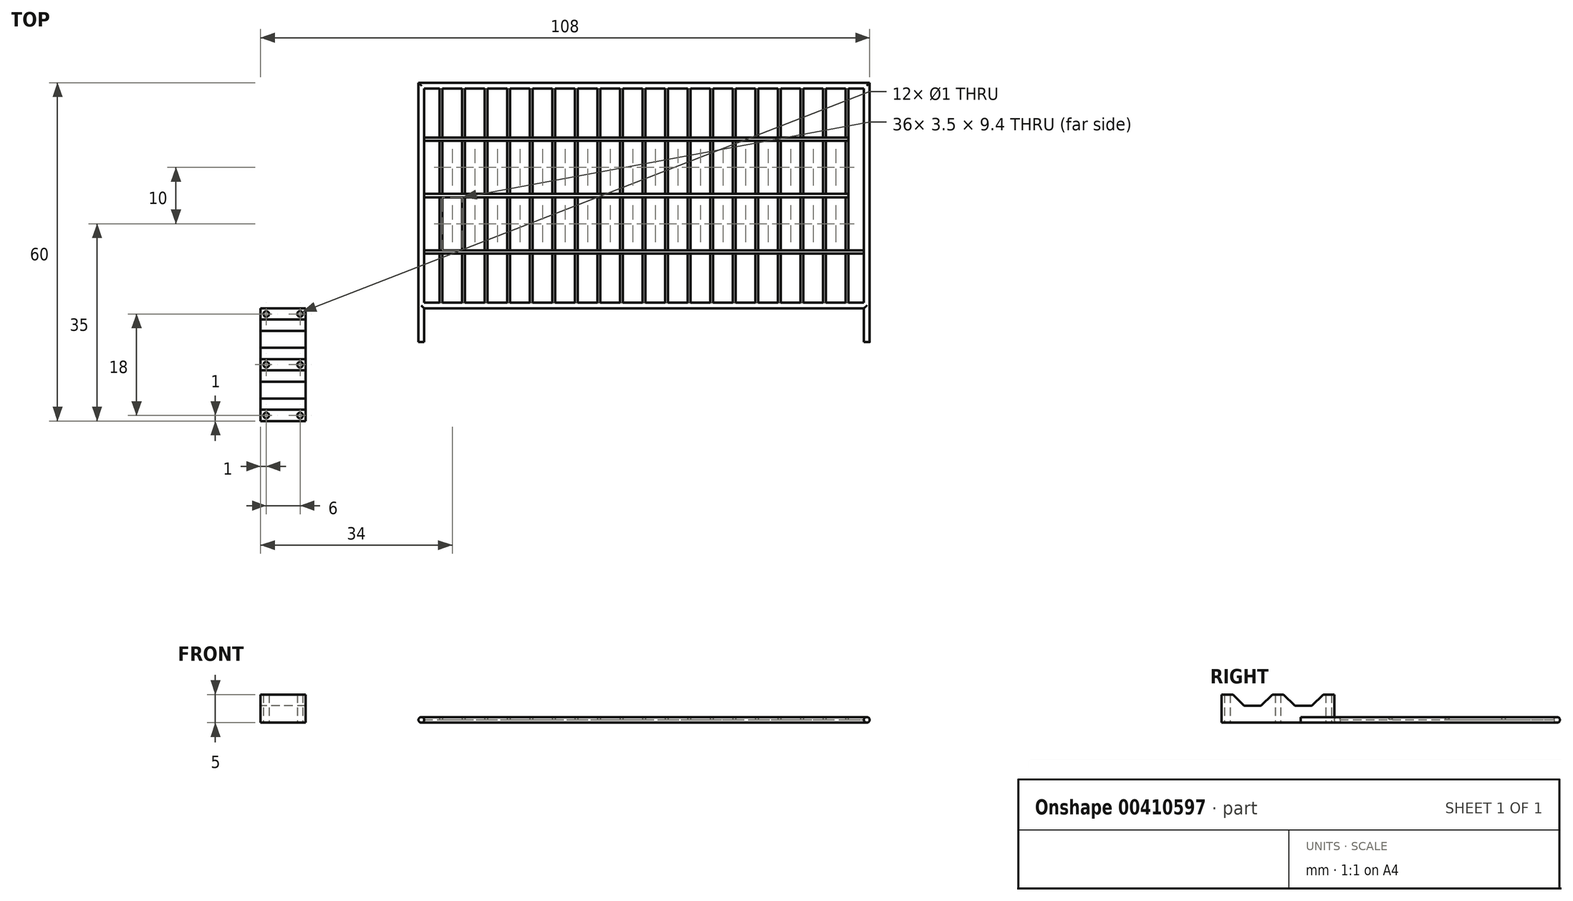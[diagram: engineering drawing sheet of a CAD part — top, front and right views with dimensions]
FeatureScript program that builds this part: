
annotation { "Feature Type Name" : "Feature", "Feature Type Description" : "" }
export const myFeature = defineFeature(function(context is Context, id is Id, definition is map)
    precondition{}
    {
        {
            var Q0;
            Q0=qCreatedBy(makeId("Top.planeOp"),FACE);
            var sketch = newSketch(context, id + "F0", { "sketchPlane" : qUnion([Q0])});
            skLineSegment(sketch, "E0.bottom", {"start": v(0, 0) * mm, "end": v(80, 0) * mm});
            skLineSegment(sketch, "E0.top", {"start": v(0, 40) * mm, "end": v(80, 40) * mm});
            skLineSegment(sketch, "E0.left", {"start": v(0, 0) * mm, "end": v(0, 40) * mm});
            skLineSegment(sketch, "E0.right", {"start": v(80, 0) * mm, "end": v(80, 40) * mm});
            skLineSegment(sketch, "E1", {"start": v(0, 0) * mm, "end": v(0, -6) * mm});
            skLineSegment(sketch, "E2", {"start": v(0, -6) * mm, "end": v(1, -6) * mm});
            skLineSegment(sketch, "E3", {"start": v(1, -6) * mm, "end": v(1, 0) * mm});
            skLineSegment(sketch, "E4", {"start": v(1, 39) * mm, "end": v(79, 39) * mm});
            skLineSegment(sketch, "E5", {"start": v(79, 39) * mm, "end": v(79, 1) * mm});
            skLineSegment(sketch, "E6", {"start": v(79, -6) * mm, "end": v(80, -6) * mm});
            skLineSegment(sketch, "E7", {"start": v(80, -6) * mm, "end": v(80, 0) * mm});
            skLineSegment(sketch, "E8", {"start": v(1, 1) * mm, "end": v(79, 1) * mm});
            skLineSegment(sketch, "E9.trimOffspring", {"start": v(79, 0) * mm, "end": v(79, -6) * mm});
            skLineSegment(sketch, "E10.trimOffspring", {"start": v(1, 1) * mm, "end": v(1, 39) * mm});
            skSolve(sketch);
        }
        {
            var Q0;
            Q0 = qSketchRegion(id + "F0", true);
            extrude(context, id + "F1", {"entities" : qUnion([Q0]), "depth" : 1 * mm});
        }
        {
            var Q0;
            Q0=makeQuery(id+"F1.opExtrude","CAP_FACE",FACE,{"disambiguationData":[OSD([sQuery(id+"F0.wireOp",EDGE,"E0.bottom"),sQuery(id+"F0.wireOp",EDGE,"E0.top"),sQuery(id+"F0.wireOp",EDGE,"E0.left"),sQuery(id+"F0.wireOp",EDGE,"E0.right"),sQuery(id+"F0.wireOp",EDGE,"E1"),sQuery(id+"F0.wireOp",EDGE,"E2"),sQuery(id+"F0.wireOp",EDGE,"E3"),sQuery(id+"F0.wireOp",EDGE,"E4"),sQuery(id+"F0.wireOp",EDGE,"E5"),sQuery(id+"F0.wireOp",EDGE,"E6"),sQuery(id+"F0.wireOp",EDGE,"E7"),sQuery(id+"F0.wireOp",EDGE,"E8"),sQuery(id+"F0.wireOp",EDGE,"E9.trimOffspring"),sQuery(id+"F0.wireOp",EDGE,"E10.trimOffspring")])],"isStart":false});
            var sketch = newSketch(context, id + "F2", { "sketchPlane" : qUnion([Q0])});
            skLineSegment(sketch, "E11", {"start": v(40, 1) * mm, "end": v(40, 39) * mm, "construction": true});
            skLineSegment(sketch, "E12", {"start": v(40.25, 1) * mm, "end": v(40.25, 39) * mm});
            skLineSegment(sketch, "E13.MirrorCS", {"start": v(39.75, 1) * mm, "end": v(39.75, 39) * mm});
            skLineSegment(sketch, "E14.1.0.0", {"start": v(44.25, 1) * mm, "end": v(44.25, 39) * mm});
            skLineSegment(sketch, "E14.1.0.1", {"start": v(43.75, 1) * mm, "end": v(43.75, 39) * mm});
            skLineSegment(sketch, "E14.2.0.0", {"start": v(48.25, 1) * mm, "end": v(48.25, 39) * mm});
            skLineSegment(sketch, "E14.2.0.1", {"start": v(47.75, 1) * mm, "end": v(47.75, 39) * mm});
            skLineSegment(sketch, "E14.3.0.0", {"start": v(52.25, 1) * mm, "end": v(52.25, 39) * mm});
            skLineSegment(sketch, "E14.3.0.1", {"start": v(51.75, 1) * mm, "end": v(51.75, 39) * mm});
            skLineSegment(sketch, "E14.4.0.0", {"start": v(56.25, 1) * mm, "end": v(56.25, 39) * mm});
            skLineSegment(sketch, "E14.4.0.1", {"start": v(55.75, 1) * mm, "end": v(55.75, 39) * mm});
            skLineSegment(sketch, "E14.5.0.0", {"start": v(60.25, 1) * mm, "end": v(60.25, 39) * mm});
            skLineSegment(sketch, "E14.5.0.1", {"start": v(59.75, 1) * mm, "end": v(59.75, 39) * mm});
            skLineSegment(sketch, "E14.6.0.0", {"start": v(64.25, 1) * mm, "end": v(64.25, 39) * mm});
            skLineSegment(sketch, "E14.6.0.1", {"start": v(63.75, 1) * mm, "end": v(63.75, 39) * mm});
            skLineSegment(sketch, "E14.7.0.0", {"start": v(68.25, 1) * mm, "end": v(68.25, 39) * mm});
            skLineSegment(sketch, "E14.7.0.1", {"start": v(67.75, 1) * mm, "end": v(67.75, 39) * mm});
            skLineSegment(sketch, "E14.8.0.0", {"start": v(72.25, 1) * mm, "end": v(72.25, 39) * mm});
            skLineSegment(sketch, "E14.8.0.1", {"start": v(71.75, 1) * mm, "end": v(71.75, 39) * mm});
            skLineSegment(sketch, "E14.9.0.0", {"start": v(76.25, 1) * mm, "end": v(76.25, 39) * mm});
            skLineSegment(sketch, "E14.9.0.1", {"start": v(75.75, 1) * mm, "end": v(75.75, 39) * mm});
            skLineSegment(sketch, "E14.direction1", {"start": v(40.25, 1) * mm, "end": v(44.25, 1) * mm, "construction": true});
            skLineSegment(sketch, "E15.MirrorCS", {"start": v(36.25, 1) * mm, "end": v(36.25, 39) * mm});
            skLineSegment(sketch, "E16.MirrorCS", {"start": v(35.75, 1) * mm, "end": v(35.75, 39) * mm});
            skLineSegment(sketch, "E17.MirrorCS", {"start": v(32.25, 1) * mm, "end": v(32.25, 39) * mm});
            skLineSegment(sketch, "E18.MirrorCS", {"start": v(31.75, 1) * mm, "end": v(31.75, 39) * mm});
            skLineSegment(sketch, "E19.MirrorCS", {"start": v(28.25, 1) * mm, "end": v(28.25, 39) * mm});
            skLineSegment(sketch, "E20.MirrorCS", {"start": v(27.75, 1) * mm, "end": v(27.75, 39) * mm});
            skLineSegment(sketch, "E21.MirrorCS", {"start": v(24.25, 1) * mm, "end": v(24.25, 39) * mm});
            skLineSegment(sketch, "E22.MirrorCS", {"start": v(23.75, 1) * mm, "end": v(23.75, 39) * mm});
            skLineSegment(sketch, "E23.MirrorCS", {"start": v(20.25, 1) * mm, "end": v(20.25, 39) * mm});
            skLineSegment(sketch, "E24.MirrorCS", {"start": v(19.75, 1) * mm, "end": v(19.75, 39) * mm});
            skLineSegment(sketch, "E25.MirrorCS", {"start": v(16.25, 1) * mm, "end": v(16.25, 39) * mm});
            skLineSegment(sketch, "E26.MirrorCS", {"start": v(15.75, 1) * mm, "end": v(15.75, 39) * mm});
            skLineSegment(sketch, "E27.MirrorCS", {"start": v(12.25, 1) * mm, "end": v(12.25, 39) * mm});
            skLineSegment(sketch, "E28.MirrorCS", {"start": v(11.75, 1) * mm, "end": v(11.75, 39) * mm});
            skLineSegment(sketch, "E29.MirrorCS", {"start": v(7.75, 1) * mm, "end": v(7.75, 39) * mm});
            skLineSegment(sketch, "E30.MirrorCS", {"start": v(8.25, 1) * mm, "end": v(8.25, 39) * mm});
            skLineSegment(sketch, "E31.MirrorCS", {"start": v(4.25, 1) * mm, "end": v(4.25, 39) * mm});
            skLineSegment(sketch, "E32.MirrorCS", {"start": v(3.75, 1) * mm, "end": v(3.75, 39) * mm});
            skLineSegment(sketch, "E33", {"start": v(3.75, 39) * mm, "end": v(76.25, 39) * mm});
            skLineSegment(sketch, "E34", {"start": v(3.75, 1) * mm, "end": v(76.25, 1) * mm});
            skSolve(sketch);
        }
        {
            var Q0;
            {var subQ0=sQuery(id+"F2.wireOp",EDGE,"E12");Q0=makeQuery(id+"F2.imprint","IMPRINT",FACE,{"disambiguationData":[TD([[makeQuery(id+"F2.imprint","IMPRINT",EDGE,{"derivedFrom":subQ0}),1.0]])]});}
            var Q1;
            {var subQ0=sQuery(id+"F2.wireOp",EDGE,"E14.1.0.0");Q1=makeQuery(id+"F2.imprint","IMPRINT",FACE,{"disambiguationData":[TD([[makeQuery(id+"F2.imprint","IMPRINT",EDGE,{"derivedFrom":subQ0}),1.0]])]});}
            var Q2;
            {var subQ0=sQuery(id+"F2.wireOp",EDGE,"E14.2.0.0");Q2=makeQuery(id+"F2.imprint","IMPRINT",FACE,{"disambiguationData":[TD([[makeQuery(id+"F2.imprint","IMPRINT",EDGE,{"derivedFrom":subQ0}),1.0]])]});}
            var Q3;
            {var subQ0=sQuery(id+"F2.wireOp",EDGE,"E14.3.0.0");Q3=makeQuery(id+"F2.imprint","IMPRINT",FACE,{"disambiguationData":[TD([[makeQuery(id+"F2.imprint","IMPRINT",EDGE,{"derivedFrom":subQ0}),1.0]])]});}
            var Q4;
            {var subQ0=sQuery(id+"F2.wireOp",EDGE,"E14.4.0.0");Q4=makeQuery(id+"F2.imprint","IMPRINT",FACE,{"disambiguationData":[TD([[makeQuery(id+"F2.imprint","IMPRINT",EDGE,{"derivedFrom":subQ0}),1.0]])]});}
            var Q5;
            {var subQ0=sQuery(id+"F2.wireOp",EDGE,"E14.5.0.0");Q5=makeQuery(id+"F2.imprint","IMPRINT",FACE,{"disambiguationData":[TD([[makeQuery(id+"F2.imprint","IMPRINT",EDGE,{"derivedFrom":subQ0}),1.0]])]});}
            var Q6;
            {var subQ0=sQuery(id+"F2.wireOp",EDGE,"E14.6.0.0");Q6=makeQuery(id+"F2.imprint","IMPRINT",FACE,{"disambiguationData":[TD([[makeQuery(id+"F2.imprint","IMPRINT",EDGE,{"derivedFrom":subQ0}),1.0]])]});}
            var Q7;
            {var subQ0=sQuery(id+"F2.wireOp",EDGE,"E14.7.0.0");Q7=makeQuery(id+"F2.imprint","IMPRINT",FACE,{"disambiguationData":[TD([[makeQuery(id+"F2.imprint","IMPRINT",EDGE,{"derivedFrom":subQ0}),1.0]])]});}
            var Q8;
            {var subQ0=sQuery(id+"F2.wireOp",EDGE,"E14.8.0.0");Q8=makeQuery(id+"F2.imprint","IMPRINT",FACE,{"disambiguationData":[TD([[makeQuery(id+"F2.imprint","IMPRINT",EDGE,{"derivedFrom":subQ0}),1.0]])]});}
            var Q9;
            {var subQ0=sQuery(id+"F2.wireOp",EDGE,"E14.9.0.0");Q9=makeQuery(id+"F2.imprint","IMPRINT",FACE,{"disambiguationData":[TD([[makeQuery(id+"F2.imprint","IMPRINT",EDGE,{"derivedFrom":subQ0}),1.0]])]});}
            var Q10;
            {var subQ0=sQuery(id+"F2.wireOp",EDGE,"E15.MirrorCS");Q10=makeQuery(id+"F2.imprint","IMPRINT",FACE,{"disambiguationData":[TD([[makeQuery(id+"F2.imprint","IMPRINT",EDGE,{"derivedFrom":subQ0}),1.0]])]});}
            var Q11;
            {var subQ0=sQuery(id+"F2.wireOp",EDGE,"E17.MirrorCS");Q11=makeQuery(id+"F2.imprint","IMPRINT",FACE,{"disambiguationData":[TD([[makeQuery(id+"F2.imprint","IMPRINT",EDGE,{"derivedFrom":subQ0}),1.0]])]});}
            var Q12;
            {var subQ0=sQuery(id+"F2.wireOp",EDGE,"E19.MirrorCS");Q12=makeQuery(id+"F2.imprint","IMPRINT",FACE,{"disambiguationData":[TD([[makeQuery(id+"F2.imprint","IMPRINT",EDGE,{"derivedFrom":subQ0}),1.0]])]});}
            var Q13;
            {var subQ0=sQuery(id+"F2.wireOp",EDGE,"E21.MirrorCS");Q13=makeQuery(id+"F2.imprint","IMPRINT",FACE,{"disambiguationData":[TD([[makeQuery(id+"F2.imprint","IMPRINT",EDGE,{"derivedFrom":subQ0}),1.0]])]});}
            var Q14;
            {var subQ0=sQuery(id+"F2.wireOp",EDGE,"E23.MirrorCS");Q14=makeQuery(id+"F2.imprint","IMPRINT",FACE,{"disambiguationData":[TD([[makeQuery(id+"F2.imprint","IMPRINT",EDGE,{"derivedFrom":subQ0}),1.0]])]});}
            var Q15;
            {var subQ0=sQuery(id+"F2.wireOp",EDGE,"E25.MirrorCS");Q15=makeQuery(id+"F2.imprint","IMPRINT",FACE,{"disambiguationData":[TD([[makeQuery(id+"F2.imprint","IMPRINT",EDGE,{"derivedFrom":subQ0}),1.0]])]});}
            var Q16;
            {var subQ0=sQuery(id+"F2.wireOp",EDGE,"E27.MirrorCS");Q16=makeQuery(id+"F2.imprint","IMPRINT",FACE,{"disambiguationData":[TD([[makeQuery(id+"F2.imprint","IMPRINT",EDGE,{"derivedFrom":subQ0}),1.0]])]});}
            var Q17;
            {var subQ0=sQuery(id+"F2.wireOp",EDGE,"E29.MirrorCS");Q17=makeQuery(id+"F2.imprint","IMPRINT",FACE,{"disambiguationData":[TD([[makeQuery(id+"F2.imprint","IMPRINT",EDGE,{"derivedFrom":subQ0}),-1.0]])]});}
            var Q18;
            {var subQ0=sQuery(id+"F2.wireOp",EDGE,"E31.MirrorCS");Q18=makeQuery(id+"F2.imprint","IMPRINT",FACE,{"disambiguationData":[TD([[makeQuery(id+"F2.imprint","IMPRINT",EDGE,{"derivedFrom":subQ0}),1.0]])]});}
            extrude(context, id + "F3", {"entities" : qUnion([Q0, Q1, Q2, Q3, Q4, Q5, Q6, Q7, Q8, Q9, Q10, Q11, Q12, Q13, Q14, Q15, Q16, Q17, Q18]), "operationType" : NewBodyOperationType.ADD, "oppositeDirection" : true, "depth" : 0.5 * mm});
        }
        {
            var Q0;
            {var subQ0=sQuery(id+"F2.wireOp",EDGE,"E34");var subQ1=sQuery(id+"F2.wireOp",EDGE,"E33");Q0=makeQuery(id+"F3.boolean.opBoolean","MERGE",FACE,{"derivedFrom":[makeQuery(id+"F1.opExtrude","CAP_FACE",FACE,{"disambiguationData":[OSD([sQuery(id+"F0.wireOp",EDGE,"E0.bottom"),sQuery(id+"F0.wireOp",EDGE,"E0.top"),sQuery(id+"F0.wireOp",EDGE,"E0.left"),sQuery(id+"F0.wireOp",EDGE,"E0.right"),sQuery(id+"F0.wireOp",EDGE,"E1"),sQuery(id+"F0.wireOp",EDGE,"E2"),sQuery(id+"F0.wireOp",EDGE,"E3"),sQuery(id+"F0.wireOp",EDGE,"E4"),sQuery(id+"F0.wireOp",EDGE,"E5"),sQuery(id+"F0.wireOp",EDGE,"E6"),sQuery(id+"F0.wireOp",EDGE,"E7"),sQuery(id+"F0.wireOp",EDGE,"E8"),sQuery(id+"F0.wireOp",EDGE,"E9.trimOffspring"),sQuery(id+"F0.wireOp",EDGE,"E10.trimOffspring")])],"isStart":false}),makeQuery(id+"F3.opExtrude","CAP_FACE",FACE,{"disambiguationData":[OSD([sQuery(id+"F2.wireOp",EDGE,"E12"),sQuery(id+"F2.wireOp",EDGE,"E13.MirrorCS"),subQ1,subQ0])],"isStart":true}),makeQuery(id+"F3.opExtrude","CAP_FACE",FACE,{"disambiguationData":[OSD([sQuery(id+"F2.wireOp",EDGE,"E14.1.0.0"),sQuery(id+"F2.wireOp",EDGE,"E14.1.0.1"),subQ1,subQ0])],"isStart":true}),makeQuery(id+"F3.opExtrude","CAP_FACE",FACE,{"disambiguationData":[OSD([sQuery(id+"F2.wireOp",EDGE,"E14.2.0.0"),sQuery(id+"F2.wireOp",EDGE,"E14.2.0.1"),subQ1,subQ0])],"isStart":true}),makeQuery(id+"F3.opExtrude","CAP_FACE",FACE,{"disambiguationData":[OSD([sQuery(id+"F2.wireOp",EDGE,"E14.3.0.0"),sQuery(id+"F2.wireOp",EDGE,"E14.3.0.1"),subQ1,subQ0])],"isStart":true}),makeQuery(id+"F3.opExtrude","CAP_FACE",FACE,{"disambiguationData":[OSD([sQuery(id+"F2.wireOp",EDGE,"E14.4.0.0"),sQuery(id+"F2.wireOp",EDGE,"E14.4.0.1"),subQ1,subQ0])],"isStart":true}),makeQuery(id+"F3.opExtrude","CAP_FACE",FACE,{"disambiguationData":[OSD([sQuery(id+"F2.wireOp",EDGE,"E14.5.0.0"),sQuery(id+"F2.wireOp",EDGE,"E14.5.0.1"),subQ1,subQ0])],"isStart":true}),makeQuery(id+"F3.opExtrude","CAP_FACE",FACE,{"disambiguationData":[OSD([sQuery(id+"F2.wireOp",EDGE,"E14.6.0.0"),sQuery(id+"F2.wireOp",EDGE,"E14.6.0.1"),subQ1,subQ0])],"isStart":true}),makeQuery(id+"F3.opExtrude","CAP_FACE",FACE,{"disambiguationData":[OSD([sQuery(id+"F2.wireOp",EDGE,"E14.7.0.0"),sQuery(id+"F2.wireOp",EDGE,"E14.7.0.1"),subQ1,subQ0])],"isStart":true}),makeQuery(id+"F3.opExtrude","CAP_FACE",FACE,{"disambiguationData":[OSD([sQuery(id+"F2.wireOp",EDGE,"E14.8.0.0"),sQuery(id+"F2.wireOp",EDGE,"E14.8.0.1"),subQ1,subQ0])],"isStart":true}),makeQuery(id+"F3.opExtrude","CAP_FACE",FACE,{"disambiguationData":[OSD([sQuery(id+"F2.wireOp",EDGE,"E14.9.0.0"),sQuery(id+"F2.wireOp",EDGE,"E14.9.0.1"),subQ1,subQ0])],"isStart":true}),makeQuery(id+"F3.opExtrude","CAP_FACE",FACE,{"disambiguationData":[OSD([sQuery(id+"F2.wireOp",EDGE,"E15.MirrorCS"),sQuery(id+"F2.wireOp",EDGE,"E16.MirrorCS"),subQ1,subQ0])],"isStart":true}),makeQuery(id+"F3.opExtrude","CAP_FACE",FACE,{"disambiguationData":[OSD([sQuery(id+"F2.wireOp",EDGE,"E17.MirrorCS"),sQuery(id+"F2.wireOp",EDGE,"E18.MirrorCS"),subQ1,subQ0])],"isStart":true}),makeQuery(id+"F3.opExtrude","CAP_FACE",FACE,{"disambiguationData":[OSD([sQuery(id+"F2.wireOp",EDGE,"E19.MirrorCS"),sQuery(id+"F2.wireOp",EDGE,"E20.MirrorCS"),subQ1,subQ0])],"isStart":true}),makeQuery(id+"F3.opExtrude","CAP_FACE",FACE,{"disambiguationData":[OSD([sQuery(id+"F2.wireOp",EDGE,"E21.MirrorCS"),sQuery(id+"F2.wireOp",EDGE,"E22.MirrorCS"),subQ1,subQ0])],"isStart":true}),makeQuery(id+"F3.opExtrude","CAP_FACE",FACE,{"disambiguationData":[OSD([sQuery(id+"F2.wireOp",EDGE,"E23.MirrorCS"),sQuery(id+"F2.wireOp",EDGE,"E24.MirrorCS"),subQ1,subQ0])],"isStart":true}),makeQuery(id+"F3.opExtrude","CAP_FACE",FACE,{"disambiguationData":[OSD([sQuery(id+"F2.wireOp",EDGE,"E25.MirrorCS"),sQuery(id+"F2.wireOp",EDGE,"E26.MirrorCS"),subQ1,subQ0])],"isStart":true}),makeQuery(id+"F3.opExtrude","CAP_FACE",FACE,{"disambiguationData":[OSD([sQuery(id+"F2.wireOp",EDGE,"E27.MirrorCS"),sQuery(id+"F2.wireOp",EDGE,"E28.MirrorCS"),subQ1,subQ0])],"isStart":true}),makeQuery(id+"F3.opExtrude","CAP_FACE",FACE,{"disambiguationData":[OSD([sQuery(id+"F2.wireOp",EDGE,"E29.MirrorCS"),sQuery(id+"F2.wireOp",EDGE,"E30.MirrorCS"),subQ1,subQ0])],"isStart":true}),makeQuery(id+"F3.opExtrude","CAP_FACE",FACE,{"disambiguationData":[OSD([sQuery(id+"F2.wireOp",EDGE,"E31.MirrorCS"),sQuery(id+"F2.wireOp",EDGE,"E32.MirrorCS"),subQ1,subQ0])],"isStart":true})]});}
            var sketch = newSketch(context, id + "F4", { "sketchPlane" : qUnion([Q0])});
            skLineSegment(sketch, "E35", {"start": v(1, 20) * mm, "end": v(79, 20) * mm, "construction": true});
            skLineSegment(sketch, "E36", {"start": v(1, 20.3) * mm, "end": v(79, 20.3) * mm});
            skLineSegment(sketch, "E37.MirrorCS", {"start": v(1, 19.7) * mm, "end": v(79, 19.7) * mm});
            skLineSegment(sketch, "E38.0.1.0", {"start": v(1, 30.3) * mm, "end": v(79, 30.3) * mm});
            skLineSegment(sketch, "E38.0.1.1", {"start": v(1, 29.7) * mm, "end": v(79, 29.7) * mm});
            skLineSegment(sketch, "E38.1.1.0", {"start": v(1, 30.3) * mm, "end": v(79, 30.3) * mm});
            skLineSegment(sketch, "E38.1.1.1", {"start": v(1, 29.7) * mm, "end": v(79, 29.7) * mm});
            skLineSegment(sketch, "E38.2.0.0", {"start": v(0.98, 20.3) * mm, "end": v(78.98, 20.3) * mm});
            skLineSegment(sketch, "E38.2.0.1", {"start": v(0.98, 19.7) * mm, "end": v(78.98, 19.7) * mm});
            skLineSegment(sketch, "E38.2.1.0", {"start": v(0.98, 30.3) * mm, "end": v(78.98, 30.3) * mm});
            skLineSegment(sketch, "E38.2.1.1", {"start": v(0.98, 29.7) * mm, "end": v(78.98, 29.7) * mm});
            skLineSegment(sketch, "E38.direction1", {"start": v(1, 19.7) * mm, "end": v(1, 19.7) * mm, "construction": true});
            skLineSegment(sketch, "E38.direction2", {"start": v(1, 19.7) * mm, "end": v(1, 29.7) * mm, "construction": true});
            skLineSegment(sketch, "E39.MirrorCS", {"start": v(0.98, 10.3) * mm, "end": v(78.98, 10.3) * mm});
            skLineSegment(sketch, "E40.MirrorCS", {"start": v(0.98, 9.7) * mm, "end": v(78.98, 9.7) * mm});
            skLineSegment(sketch, "E41", {"start": v(1, 30.3) * mm, "end": v(1, 29.7) * mm});
            skLineSegment(sketch, "E42", {"start": v(1, 20.3) * mm, "end": v(1, 19.7) * mm});
            skLineSegment(sketch, "E43", {"start": v(0.98, 10.3) * mm, "end": v(0.98, 9.7) * mm});
            skLineSegment(sketch, "E44", {"start": v(79, 30.3) * mm, "end": v(79, 29.7) * mm});
            skLineSegment(sketch, "E45", {"start": v(79, 20.3) * mm, "end": v(79, 19.7) * mm});
            skLineSegment(sketch, "E46", {"start": v(78.98, 9.7) * mm, "end": v(78.98, 10.3) * mm});
            skSolve(sketch);
        }
        {
            var Q0;
            {var subQ0=sQuery(id+"F4.wireOp",EDGE,"E38.0.1.1");var subQ1=makeQuery(id+"F3.opExtrude","CAP_EDGE",EDGE,{"disambiguationData":[OSD([sQuery(id+"F2.wireOp",EDGE,"E30.MirrorCS")])],"isStart":true});var subQ2=makeQuery(id+"F4.imprint","INTERSECT",VERTEX,{"derivedFrom":[subQ1,subQ0]});Q0=makeQuery(id+"F4.imprint","IMPRINT",FACE,{"disambiguationData":[TD([[makeQuery(id+"F4.imprint","IMPRINT",EDGE,{"disambiguationData":[TD([[subQ2,-1.0]])],"derivedFrom":subQ0}),1.0]])]});}
            var Q1;
            {var subQ0=sQuery(id+"F4.wireOp",EDGE,"E38.0.1.1");var subQ1=makeQuery(id+"F3.opExtrude","CAP_EDGE",EDGE,{"disambiguationData":[OSD([sQuery(id+"F2.wireOp",EDGE,"E31.MirrorCS")])],"isStart":true});var subQ2=makeQuery(id+"F4.imprint","INTERSECT",VERTEX,{"derivedFrom":[subQ1,subQ0]});Q1=makeQuery(id+"F4.imprint","IMPRINT",FACE,{"disambiguationData":[TD([[makeQuery(id+"F4.imprint","IMPRINT",EDGE,{"disambiguationData":[TD([[subQ2,-1.0]])],"derivedFrom":subQ0}),1.0]])]});}
            var Q2;
            {var subQ0=sQuery(id+"F4.wireOp",EDGE,"E41");var subQ5=sQuery(id+"F4.wireOp",EDGE,"E38.2.1.0");var subQ6=makeQuery(id+"F4.imprint","INTERSECT",VERTEX,{"derivedFrom":[subQ5,subQ0]});Q2=makeQuery(id+"F4.imprint","IMPRINT",FACE,{"disambiguationData":[TD([[makeQuery(id+"F4.imprint","IMPRINT",EDGE,{"disambiguationData":[TD([[subQ6,-1.0]])],"derivedFrom":subQ5}),-1.0]])]});}
            var Q3;
            {var subQ0=sQuery(id+"F4.wireOp",EDGE,"E38.0.1.1");var subQ1=makeQuery(id+"F3.opExtrude","CAP_EDGE",EDGE,{"disambiguationData":[OSD([sQuery(id+"F2.wireOp",EDGE,"E27.MirrorCS")])],"isStart":true});var subQ2=makeQuery(id+"F4.imprint","INTERSECT",VERTEX,{"derivedFrom":[subQ1,subQ0]});Q3=makeQuery(id+"F4.imprint","IMPRINT",FACE,{"disambiguationData":[TD([[makeQuery(id+"F4.imprint","IMPRINT",EDGE,{"disambiguationData":[TD([[subQ2,-1.0]])],"derivedFrom":subQ0}),1.0]])]});}
            var Q4;
            {var subQ0=sQuery(id+"F4.wireOp",EDGE,"E38.0.1.1");var subQ1=makeQuery(id+"F3.opExtrude","CAP_EDGE",EDGE,{"disambiguationData":[OSD([sQuery(id+"F2.wireOp",EDGE,"E25.MirrorCS")])],"isStart":true});var subQ2=makeQuery(id+"F4.imprint","INTERSECT",VERTEX,{"derivedFrom":[subQ1,subQ0]});Q4=makeQuery(id+"F4.imprint","IMPRINT",FACE,{"disambiguationData":[TD([[makeQuery(id+"F4.imprint","IMPRINT",EDGE,{"disambiguationData":[TD([[subQ2,-1.0]])],"derivedFrom":subQ0}),1.0]])]});}
            var Q5;
            {var subQ0=sQuery(id+"F4.wireOp",EDGE,"E38.0.1.1");var subQ1=makeQuery(id+"F3.opExtrude","CAP_EDGE",EDGE,{"disambiguationData":[OSD([sQuery(id+"F2.wireOp",EDGE,"E23.MirrorCS")])],"isStart":true});var subQ2=makeQuery(id+"F4.imprint","INTERSECT",VERTEX,{"derivedFrom":[subQ1,subQ0]});Q5=makeQuery(id+"F4.imprint","IMPRINT",FACE,{"disambiguationData":[TD([[makeQuery(id+"F4.imprint","IMPRINT",EDGE,{"disambiguationData":[TD([[subQ2,-1.0]])],"derivedFrom":subQ0}),1.0]])]});}
            var Q6;
            {var subQ0=sQuery(id+"F4.wireOp",EDGE,"E38.0.1.1");var subQ1=makeQuery(id+"F3.opExtrude","CAP_EDGE",EDGE,{"disambiguationData":[OSD([sQuery(id+"F2.wireOp",EDGE,"E21.MirrorCS")])],"isStart":true});var subQ2=makeQuery(id+"F4.imprint","INTERSECT",VERTEX,{"derivedFrom":[subQ1,subQ0]});Q6=makeQuery(id+"F4.imprint","IMPRINT",FACE,{"disambiguationData":[TD([[makeQuery(id+"F4.imprint","IMPRINT",EDGE,{"disambiguationData":[TD([[subQ2,-1.0]])],"derivedFrom":subQ0}),1.0]])]});}
            var Q7;
            {var subQ0=sQuery(id+"F4.wireOp",EDGE,"E38.0.1.1");var subQ1=makeQuery(id+"F3.opExtrude","CAP_EDGE",EDGE,{"disambiguationData":[OSD([sQuery(id+"F2.wireOp",EDGE,"E19.MirrorCS")])],"isStart":true});var subQ2=makeQuery(id+"F4.imprint","INTERSECT",VERTEX,{"derivedFrom":[subQ1,subQ0]});Q7=makeQuery(id+"F4.imprint","IMPRINT",FACE,{"disambiguationData":[TD([[makeQuery(id+"F4.imprint","IMPRINT",EDGE,{"disambiguationData":[TD([[subQ2,-1.0]])],"derivedFrom":subQ0}),1.0]])]});}
            var Q8;
            {var subQ0=sQuery(id+"F4.wireOp",EDGE,"E38.0.1.1");var subQ1=makeQuery(id+"F3.opExtrude","CAP_EDGE",EDGE,{"disambiguationData":[OSD([sQuery(id+"F2.wireOp",EDGE,"E17.MirrorCS")])],"isStart":true});var subQ2=makeQuery(id+"F4.imprint","INTERSECT",VERTEX,{"derivedFrom":[subQ1,subQ0]});Q8=makeQuery(id+"F4.imprint","IMPRINT",FACE,{"disambiguationData":[TD([[makeQuery(id+"F4.imprint","IMPRINT",EDGE,{"disambiguationData":[TD([[subQ2,-1.0]])],"derivedFrom":subQ0}),1.0]])]});}
            var Q9;
            {var subQ0=sQuery(id+"F4.wireOp",EDGE,"E38.0.1.1");var subQ1=makeQuery(id+"F3.opExtrude","CAP_EDGE",EDGE,{"disambiguationData":[OSD([sQuery(id+"F2.wireOp",EDGE,"E15.MirrorCS")])],"isStart":true});var subQ2=makeQuery(id+"F4.imprint","INTERSECT",VERTEX,{"derivedFrom":[subQ1,subQ0]});Q9=makeQuery(id+"F4.imprint","IMPRINT",FACE,{"disambiguationData":[TD([[makeQuery(id+"F4.imprint","IMPRINT",EDGE,{"disambiguationData":[TD([[subQ2,-1.0]])],"derivedFrom":subQ0}),1.0]])]});}
            var Q10;
            {var subQ0=sQuery(id+"F4.wireOp",EDGE,"E38.0.1.1");var subQ1=makeQuery(id+"F3.opExtrude","CAP_EDGE",EDGE,{"disambiguationData":[OSD([sQuery(id+"F2.wireOp",EDGE,"E12")])],"isStart":true});var subQ2=makeQuery(id+"F4.imprint","INTERSECT",VERTEX,{"derivedFrom":[subQ1,subQ0]});Q10=makeQuery(id+"F4.imprint","IMPRINT",FACE,{"disambiguationData":[TD([[makeQuery(id+"F4.imprint","IMPRINT",EDGE,{"disambiguationData":[TD([[subQ2,-1.0]])],"derivedFrom":subQ0}),1.0]])]});}
            var Q11;
            {var subQ0=sQuery(id+"F4.wireOp",EDGE,"E38.0.1.1");var subQ1=makeQuery(id+"F3.opExtrude","CAP_EDGE",EDGE,{"disambiguationData":[OSD([sQuery(id+"F2.wireOp",EDGE,"E14.1.0.0")])],"isStart":true});var subQ2=makeQuery(id+"F4.imprint","INTERSECT",VERTEX,{"derivedFrom":[subQ1,subQ0]});Q11=makeQuery(id+"F4.imprint","IMPRINT",FACE,{"disambiguationData":[TD([[makeQuery(id+"F4.imprint","IMPRINT",EDGE,{"disambiguationData":[TD([[subQ2,-1.0]])],"derivedFrom":subQ0}),1.0]])]});}
            var Q12;
            {var subQ0=sQuery(id+"F4.wireOp",EDGE,"E38.0.1.1");var subQ1=makeQuery(id+"F3.opExtrude","CAP_EDGE",EDGE,{"disambiguationData":[OSD([sQuery(id+"F2.wireOp",EDGE,"E14.2.0.0")])],"isStart":true});var subQ2=makeQuery(id+"F4.imprint","INTERSECT",VERTEX,{"derivedFrom":[subQ1,subQ0]});Q12=makeQuery(id+"F4.imprint","IMPRINT",FACE,{"disambiguationData":[TD([[makeQuery(id+"F4.imprint","IMPRINT",EDGE,{"disambiguationData":[TD([[subQ2,-1.0]])],"derivedFrom":subQ0}),1.0]])]});}
            var Q13;
            {var subQ0=sQuery(id+"F4.wireOp",EDGE,"E38.0.1.1");var subQ1=makeQuery(id+"F3.opExtrude","CAP_EDGE",EDGE,{"disambiguationData":[OSD([sQuery(id+"F2.wireOp",EDGE,"E14.3.0.0")])],"isStart":true});var subQ2=makeQuery(id+"F4.imprint","INTERSECT",VERTEX,{"derivedFrom":[subQ1,subQ0]});Q13=makeQuery(id+"F4.imprint","IMPRINT",FACE,{"disambiguationData":[TD([[makeQuery(id+"F4.imprint","IMPRINT",EDGE,{"disambiguationData":[TD([[subQ2,-1.0]])],"derivedFrom":subQ0}),1.0]])]});}
            var Q14;
            {var subQ0=sQuery(id+"F4.wireOp",EDGE,"E38.0.1.1");var subQ1=makeQuery(id+"F3.opExtrude","CAP_EDGE",EDGE,{"disambiguationData":[OSD([sQuery(id+"F2.wireOp",EDGE,"E14.4.0.0")])],"isStart":true});var subQ2=makeQuery(id+"F4.imprint","INTERSECT",VERTEX,{"derivedFrom":[subQ1,subQ0]});Q14=makeQuery(id+"F4.imprint","IMPRINT",FACE,{"disambiguationData":[TD([[makeQuery(id+"F4.imprint","IMPRINT",EDGE,{"disambiguationData":[TD([[subQ2,-1.0]])],"derivedFrom":subQ0}),1.0]])]});}
            var Q15;
            {var subQ0=sQuery(id+"F4.wireOp",EDGE,"E38.0.1.1");var subQ1=makeQuery(id+"F3.opExtrude","CAP_EDGE",EDGE,{"disambiguationData":[OSD([sQuery(id+"F2.wireOp",EDGE,"E14.5.0.0")])],"isStart":true});var subQ2=makeQuery(id+"F4.imprint","INTERSECT",VERTEX,{"derivedFrom":[subQ1,subQ0]});Q15=makeQuery(id+"F4.imprint","IMPRINT",FACE,{"disambiguationData":[TD([[makeQuery(id+"F4.imprint","IMPRINT",EDGE,{"disambiguationData":[TD([[subQ2,-1.0]])],"derivedFrom":subQ0}),1.0]])]});}
            var Q16;
            {var subQ0=sQuery(id+"F4.wireOp",EDGE,"E38.0.1.1");var subQ1=makeQuery(id+"F3.opExtrude","CAP_EDGE",EDGE,{"disambiguationData":[OSD([sQuery(id+"F2.wireOp",EDGE,"E14.6.0.0")])],"isStart":true});var subQ2=makeQuery(id+"F4.imprint","INTERSECT",VERTEX,{"derivedFrom":[subQ1,subQ0]});Q16=makeQuery(id+"F4.imprint","IMPRINT",FACE,{"disambiguationData":[TD([[makeQuery(id+"F4.imprint","IMPRINT",EDGE,{"disambiguationData":[TD([[subQ2,-1.0]])],"derivedFrom":subQ0}),1.0]])]});}
            var Q17;
            {var subQ0=sQuery(id+"F4.wireOp",EDGE,"E38.0.1.1");var subQ1=makeQuery(id+"F3.opExtrude","CAP_EDGE",EDGE,{"disambiguationData":[OSD([sQuery(id+"F2.wireOp",EDGE,"E14.7.0.0")])],"isStart":true});var subQ2=makeQuery(id+"F4.imprint","INTERSECT",VERTEX,{"derivedFrom":[subQ1,subQ0]});Q17=makeQuery(id+"F4.imprint","IMPRINT",FACE,{"disambiguationData":[TD([[makeQuery(id+"F4.imprint","IMPRINT",EDGE,{"disambiguationData":[TD([[subQ2,-1.0]])],"derivedFrom":subQ0}),1.0]])]});}
            var Q18;
            {var subQ0=sQuery(id+"F4.wireOp",EDGE,"E38.1.1.0");Q18=makeQuery(id+"F4.imprint","IMPRINT",FACE,{"disambiguationData":[TD([[makeQuery(id+"F4.imprint","IMPRINT",EDGE,{"derivedFrom":subQ0}),-1.0]])]});}
            var Q19;
            {var subQ0=sQuery(id+"F4.wireOp",EDGE,"E38.0.1.1");var subQ1=makeQuery(id+"F3.opExtrude","CAP_EDGE",EDGE,{"disambiguationData":[OSD([sQuery(id+"F2.wireOp",EDGE,"E14.8.0.0")])],"isStart":true});var subQ2=makeQuery(id+"F4.imprint","INTERSECT",VERTEX,{"derivedFrom":[subQ1,subQ0]});Q19=makeQuery(id+"F4.imprint","IMPRINT",FACE,{"disambiguationData":[TD([[makeQuery(id+"F4.imprint","IMPRINT",EDGE,{"disambiguationData":[TD([[subQ2,-1.0]])],"derivedFrom":subQ0}),1.0]])]});}
            var Q20;
            {var subQ0=sQuery(id+"F4.wireOp",EDGE,"E36");Q20=makeQuery(id+"F4.imprint","IMPRINT",FACE,{"disambiguationData":[TD([[makeQuery(id+"F4.imprint","IMPRINT",EDGE,{"derivedFrom":subQ0}),-1.0]])]});}
            var Q21;
            {var subQ0=sQuery(id+"F4.wireOp",EDGE,"E37.MirrorCS");var subQ1=makeQuery(id+"F3.opExtrude","CAP_EDGE",EDGE,{"disambiguationData":[OSD([sQuery(id+"F2.wireOp",EDGE,"E14.8.0.0")])],"isStart":true});var subQ2=makeQuery(id+"F4.imprint","INTERSECT",VERTEX,{"derivedFrom":[subQ1,subQ0]});Q21=makeQuery(id+"F4.imprint","IMPRINT",FACE,{"disambiguationData":[TD([[makeQuery(id+"F4.imprint","IMPRINT",EDGE,{"disambiguationData":[TD([[subQ2,-1.0]])],"derivedFrom":subQ0}),1.0]])]});}
            var Q22;
            {var subQ0=sQuery(id+"F4.wireOp",EDGE,"E37.MirrorCS");var subQ1=makeQuery(id+"F3.opExtrude","CAP_EDGE",EDGE,{"disambiguationData":[OSD([sQuery(id+"F2.wireOp",EDGE,"E14.7.0.0")])],"isStart":true});var subQ2=makeQuery(id+"F4.imprint","INTERSECT",VERTEX,{"derivedFrom":[subQ1,subQ0]});Q22=makeQuery(id+"F4.imprint","IMPRINT",FACE,{"disambiguationData":[TD([[makeQuery(id+"F4.imprint","IMPRINT",EDGE,{"disambiguationData":[TD([[subQ2,-1.0]])],"derivedFrom":subQ0}),1.0]])]});}
            var Q23;
            {var subQ0=sQuery(id+"F4.wireOp",EDGE,"E37.MirrorCS");var subQ1=makeQuery(id+"F3.opExtrude","CAP_EDGE",EDGE,{"disambiguationData":[OSD([sQuery(id+"F2.wireOp",EDGE,"E14.6.0.0")])],"isStart":true});var subQ2=makeQuery(id+"F4.imprint","INTERSECT",VERTEX,{"derivedFrom":[subQ1,subQ0]});Q23=makeQuery(id+"F4.imprint","IMPRINT",FACE,{"disambiguationData":[TD([[makeQuery(id+"F4.imprint","IMPRINT",EDGE,{"disambiguationData":[TD([[subQ2,-1.0]])],"derivedFrom":subQ0}),1.0]])]});}
            var Q24;
            {var subQ0=sQuery(id+"F4.wireOp",EDGE,"E37.MirrorCS");var subQ1=makeQuery(id+"F3.opExtrude","CAP_EDGE",EDGE,{"disambiguationData":[OSD([sQuery(id+"F2.wireOp",EDGE,"E14.5.0.0")])],"isStart":true});var subQ2=makeQuery(id+"F4.imprint","INTERSECT",VERTEX,{"derivedFrom":[subQ1,subQ0]});Q24=makeQuery(id+"F4.imprint","IMPRINT",FACE,{"disambiguationData":[TD([[makeQuery(id+"F4.imprint","IMPRINT",EDGE,{"disambiguationData":[TD([[subQ2,-1.0]])],"derivedFrom":subQ0}),1.0]])]});}
            var Q25;
            {var subQ0=sQuery(id+"F4.wireOp",EDGE,"E37.MirrorCS");var subQ1=makeQuery(id+"F3.opExtrude","CAP_EDGE",EDGE,{"disambiguationData":[OSD([sQuery(id+"F2.wireOp",EDGE,"E14.4.0.0")])],"isStart":true});var subQ2=makeQuery(id+"F4.imprint","INTERSECT",VERTEX,{"derivedFrom":[subQ1,subQ0]});Q25=makeQuery(id+"F4.imprint","IMPRINT",FACE,{"disambiguationData":[TD([[makeQuery(id+"F4.imprint","IMPRINT",EDGE,{"disambiguationData":[TD([[subQ2,-1.0]])],"derivedFrom":subQ0}),1.0]])]});}
            var Q26;
            {var subQ0=sQuery(id+"F4.wireOp",EDGE,"E37.MirrorCS");var subQ1=makeQuery(id+"F3.opExtrude","CAP_EDGE",EDGE,{"disambiguationData":[OSD([sQuery(id+"F2.wireOp",EDGE,"E14.3.0.0")])],"isStart":true});var subQ2=makeQuery(id+"F4.imprint","INTERSECT",VERTEX,{"derivedFrom":[subQ1,subQ0]});Q26=makeQuery(id+"F4.imprint","IMPRINT",FACE,{"disambiguationData":[TD([[makeQuery(id+"F4.imprint","IMPRINT",EDGE,{"disambiguationData":[TD([[subQ2,-1.0]])],"derivedFrom":subQ0}),1.0]])]});}
            var Q27;
            {var subQ0=sQuery(id+"F4.wireOp",EDGE,"E37.MirrorCS");var subQ1=makeQuery(id+"F3.opExtrude","CAP_EDGE",EDGE,{"disambiguationData":[OSD([sQuery(id+"F2.wireOp",EDGE,"E14.2.0.0")])],"isStart":true});var subQ2=makeQuery(id+"F4.imprint","INTERSECT",VERTEX,{"derivedFrom":[subQ1,subQ0]});Q27=makeQuery(id+"F4.imprint","IMPRINT",FACE,{"disambiguationData":[TD([[makeQuery(id+"F4.imprint","IMPRINT",EDGE,{"disambiguationData":[TD([[subQ2,-1.0]])],"derivedFrom":subQ0}),1.0]])]});}
            var Q28;
            {var subQ0=sQuery(id+"F4.wireOp",EDGE,"E37.MirrorCS");var subQ1=makeQuery(id+"F3.opExtrude","CAP_EDGE",EDGE,{"disambiguationData":[OSD([sQuery(id+"F2.wireOp",EDGE,"E14.1.0.0")])],"isStart":true});var subQ2=makeQuery(id+"F4.imprint","INTERSECT",VERTEX,{"derivedFrom":[subQ1,subQ0]});Q28=makeQuery(id+"F4.imprint","IMPRINT",FACE,{"disambiguationData":[TD([[makeQuery(id+"F4.imprint","IMPRINT",EDGE,{"disambiguationData":[TD([[subQ2,-1.0]])],"derivedFrom":subQ0}),1.0]])]});}
            var Q29;
            {var subQ0=sQuery(id+"F4.wireOp",EDGE,"E37.MirrorCS");var subQ1=makeQuery(id+"F3.opExtrude","CAP_EDGE",EDGE,{"disambiguationData":[OSD([sQuery(id+"F2.wireOp",EDGE,"E12")])],"isStart":true});var subQ2=makeQuery(id+"F4.imprint","INTERSECT",VERTEX,{"derivedFrom":[subQ1,subQ0]});Q29=makeQuery(id+"F4.imprint","IMPRINT",FACE,{"disambiguationData":[TD([[makeQuery(id+"F4.imprint","IMPRINT",EDGE,{"disambiguationData":[TD([[subQ2,-1.0]])],"derivedFrom":subQ0}),1.0]])]});}
            var Q30;
            {var subQ0=sQuery(id+"F4.wireOp",EDGE,"E37.MirrorCS");var subQ1=makeQuery(id+"F3.opExtrude","CAP_EDGE",EDGE,{"disambiguationData":[OSD([sQuery(id+"F2.wireOp",EDGE,"E15.MirrorCS")])],"isStart":true});var subQ2=makeQuery(id+"F4.imprint","INTERSECT",VERTEX,{"derivedFrom":[subQ1,subQ0]});Q30=makeQuery(id+"F4.imprint","IMPRINT",FACE,{"disambiguationData":[TD([[makeQuery(id+"F4.imprint","IMPRINT",EDGE,{"disambiguationData":[TD([[subQ2,-1.0]])],"derivedFrom":subQ0}),1.0]])]});}
            var Q31;
            {var subQ0=sQuery(id+"F4.wireOp",EDGE,"E37.MirrorCS");var subQ1=makeQuery(id+"F3.opExtrude","CAP_EDGE",EDGE,{"disambiguationData":[OSD([sQuery(id+"F2.wireOp",EDGE,"E17.MirrorCS")])],"isStart":true});var subQ2=makeQuery(id+"F4.imprint","INTERSECT",VERTEX,{"derivedFrom":[subQ1,subQ0]});Q31=makeQuery(id+"F4.imprint","IMPRINT",FACE,{"disambiguationData":[TD([[makeQuery(id+"F4.imprint","IMPRINT",EDGE,{"disambiguationData":[TD([[subQ2,-1.0]])],"derivedFrom":subQ0}),1.0]])]});}
            var Q32;
            {var subQ0=sQuery(id+"F4.wireOp",EDGE,"E37.MirrorCS");var subQ1=makeQuery(id+"F3.opExtrude","CAP_EDGE",EDGE,{"disambiguationData":[OSD([sQuery(id+"F2.wireOp",EDGE,"E19.MirrorCS")])],"isStart":true});var subQ2=makeQuery(id+"F4.imprint","INTERSECT",VERTEX,{"derivedFrom":[subQ1,subQ0]});Q32=makeQuery(id+"F4.imprint","IMPRINT",FACE,{"disambiguationData":[TD([[makeQuery(id+"F4.imprint","IMPRINT",EDGE,{"disambiguationData":[TD([[subQ2,-1.0]])],"derivedFrom":subQ0}),1.0]])]});}
            var Q33;
            {var subQ0=sQuery(id+"F4.wireOp",EDGE,"E37.MirrorCS");var subQ1=makeQuery(id+"F3.opExtrude","CAP_EDGE",EDGE,{"disambiguationData":[OSD([sQuery(id+"F2.wireOp",EDGE,"E21.MirrorCS")])],"isStart":true});var subQ2=makeQuery(id+"F4.imprint","INTERSECT",VERTEX,{"derivedFrom":[subQ1,subQ0]});Q33=makeQuery(id+"F4.imprint","IMPRINT",FACE,{"disambiguationData":[TD([[makeQuery(id+"F4.imprint","IMPRINT",EDGE,{"disambiguationData":[TD([[subQ2,-1.0]])],"derivedFrom":subQ0}),1.0]])]});}
            var Q34;
            {var subQ0=sQuery(id+"F4.wireOp",EDGE,"E37.MirrorCS");var subQ1=makeQuery(id+"F3.opExtrude","CAP_EDGE",EDGE,{"disambiguationData":[OSD([sQuery(id+"F2.wireOp",EDGE,"E23.MirrorCS")])],"isStart":true});var subQ2=makeQuery(id+"F4.imprint","INTERSECT",VERTEX,{"derivedFrom":[subQ1,subQ0]});Q34=makeQuery(id+"F4.imprint","IMPRINT",FACE,{"disambiguationData":[TD([[makeQuery(id+"F4.imprint","IMPRINT",EDGE,{"disambiguationData":[TD([[subQ2,-1.0]])],"derivedFrom":subQ0}),1.0]])]});}
            var Q35;
            {var subQ0=sQuery(id+"F4.wireOp",EDGE,"E37.MirrorCS");var subQ1=makeQuery(id+"F3.opExtrude","CAP_EDGE",EDGE,{"disambiguationData":[OSD([sQuery(id+"F2.wireOp",EDGE,"E25.MirrorCS")])],"isStart":true});var subQ2=makeQuery(id+"F4.imprint","INTERSECT",VERTEX,{"derivedFrom":[subQ1,subQ0]});Q35=makeQuery(id+"F4.imprint","IMPRINT",FACE,{"disambiguationData":[TD([[makeQuery(id+"F4.imprint","IMPRINT",EDGE,{"disambiguationData":[TD([[subQ2,-1.0]])],"derivedFrom":subQ0}),1.0]])]});}
            var Q36;
            {var subQ0=sQuery(id+"F4.wireOp",EDGE,"E37.MirrorCS");var subQ1=makeQuery(id+"F3.opExtrude","CAP_EDGE",EDGE,{"disambiguationData":[OSD([sQuery(id+"F2.wireOp",EDGE,"E27.MirrorCS")])],"isStart":true});var subQ2=makeQuery(id+"F4.imprint","INTERSECT",VERTEX,{"derivedFrom":[subQ1,subQ0]});Q36=makeQuery(id+"F4.imprint","IMPRINT",FACE,{"disambiguationData":[TD([[makeQuery(id+"F4.imprint","IMPRINT",EDGE,{"disambiguationData":[TD([[subQ2,-1.0]])],"derivedFrom":subQ0}),1.0]])]});}
            var Q37;
            {var subQ0=sQuery(id+"F4.wireOp",EDGE,"E37.MirrorCS");var subQ1=makeQuery(id+"F3.opExtrude","CAP_EDGE",EDGE,{"disambiguationData":[OSD([sQuery(id+"F2.wireOp",EDGE,"E30.MirrorCS")])],"isStart":true});var subQ2=makeQuery(id+"F4.imprint","INTERSECT",VERTEX,{"derivedFrom":[subQ1,subQ0]});Q37=makeQuery(id+"F4.imprint","IMPRINT",FACE,{"disambiguationData":[TD([[makeQuery(id+"F4.imprint","IMPRINT",EDGE,{"disambiguationData":[TD([[subQ2,-1.0]])],"derivedFrom":subQ0}),1.0]])]});}
            var Q38;
            {var subQ0=sQuery(id+"F4.wireOp",EDGE,"E37.MirrorCS");var subQ1=makeQuery(id+"F3.opExtrude","CAP_EDGE",EDGE,{"disambiguationData":[OSD([sQuery(id+"F2.wireOp",EDGE,"E31.MirrorCS")])],"isStart":true});var subQ2=makeQuery(id+"F4.imprint","INTERSECT",VERTEX,{"derivedFrom":[subQ1,subQ0]});Q38=makeQuery(id+"F4.imprint","IMPRINT",FACE,{"disambiguationData":[TD([[makeQuery(id+"F4.imprint","IMPRINT",EDGE,{"disambiguationData":[TD([[subQ2,-1.0]])],"derivedFrom":subQ0}),1.0]])]});}
            var Q39;
            {var subQ0=sQuery(id+"F4.wireOp",EDGE,"E42");var subQ5=sQuery(id+"F4.wireOp",EDGE,"E38.2.0.0");var subQ6=makeQuery(id+"F4.imprint","INTERSECT",VERTEX,{"derivedFrom":[subQ5,subQ0]});Q39=makeQuery(id+"F4.imprint","IMPRINT",FACE,{"disambiguationData":[TD([[makeQuery(id+"F4.imprint","IMPRINT",EDGE,{"disambiguationData":[TD([[subQ6,-1.0]])],"derivedFrom":subQ5}),-1.0]])]});}
            var Q40;
            {var subQ0=sQuery(id+"F4.wireOp",EDGE,"E39.MirrorCS");var subQ1=makeQuery(id+"F3.opExtrude","CAP_EDGE",EDGE,{"disambiguationData":[OSD([sQuery(id+"F2.wireOp",EDGE,"E31.MirrorCS")])],"isStart":true});var subQ2=makeQuery(id+"F4.imprint","INTERSECT",VERTEX,{"derivedFrom":[subQ1,subQ0]});Q40=makeQuery(id+"F4.imprint","IMPRINT",FACE,{"disambiguationData":[TD([[makeQuery(id+"F4.imprint","IMPRINT",EDGE,{"disambiguationData":[TD([[subQ2,-1.0]])],"derivedFrom":subQ0}),-1.0]])]});}
            var Q41;
            {var subQ0=sQuery(id+"F4.wireOp",EDGE,"E39.MirrorCS");var subQ1=makeQuery(id+"F1.opExtrude","CAP_EDGE",EDGE,{"disambiguationData":[OSD([sQuery(id+"F0.wireOp",EDGE,"E10.trimOffspring")])],"isStart":false});var subQ2=makeQuery(id+"F4.imprint","INTERSECT",VERTEX,{"derivedFrom":[subQ1,subQ0]});Q41=makeQuery(id+"F4.imprint","IMPRINT",FACE,{"disambiguationData":[TD([[makeQuery(id+"F4.imprint","IMPRINT",EDGE,{"disambiguationData":[TD([[subQ2,-1.0]])],"derivedFrom":subQ0}),-1.0]])]});}
            var Q42;
            {var subQ0=sQuery(id+"F4.wireOp",EDGE,"E39.MirrorCS");var subQ1=makeQuery(id+"F3.opExtrude","CAP_EDGE",EDGE,{"disambiguationData":[OSD([sQuery(id+"F2.wireOp",EDGE,"E30.MirrorCS")])],"isStart":true});var subQ2=makeQuery(id+"F4.imprint","INTERSECT",VERTEX,{"derivedFrom":[subQ1,subQ0]});Q42=makeQuery(id+"F4.imprint","IMPRINT",FACE,{"disambiguationData":[TD([[makeQuery(id+"F4.imprint","IMPRINT",EDGE,{"disambiguationData":[TD([[subQ2,-1.0]])],"derivedFrom":subQ0}),-1.0]])]});}
            var Q43;
            {var subQ0=sQuery(id+"F4.wireOp",EDGE,"E39.MirrorCS");var subQ1=makeQuery(id+"F3.opExtrude","CAP_EDGE",EDGE,{"disambiguationData":[OSD([sQuery(id+"F2.wireOp",EDGE,"E27.MirrorCS")])],"isStart":true});var subQ2=makeQuery(id+"F4.imprint","INTERSECT",VERTEX,{"derivedFrom":[subQ1,subQ0]});Q43=makeQuery(id+"F4.imprint","IMPRINT",FACE,{"disambiguationData":[TD([[makeQuery(id+"F4.imprint","IMPRINT",EDGE,{"disambiguationData":[TD([[subQ2,-1.0]])],"derivedFrom":subQ0}),-1.0]])]});}
            var Q44;
            {var subQ0=sQuery(id+"F4.wireOp",EDGE,"E39.MirrorCS");var subQ1=makeQuery(id+"F3.opExtrude","CAP_EDGE",EDGE,{"disambiguationData":[OSD([sQuery(id+"F2.wireOp",EDGE,"E25.MirrorCS")])],"isStart":true});var subQ2=makeQuery(id+"F4.imprint","INTERSECT",VERTEX,{"derivedFrom":[subQ1,subQ0]});Q44=makeQuery(id+"F4.imprint","IMPRINT",FACE,{"disambiguationData":[TD([[makeQuery(id+"F4.imprint","IMPRINT",EDGE,{"disambiguationData":[TD([[subQ2,-1.0]])],"derivedFrom":subQ0}),-1.0]])]});}
            var Q45;
            {var subQ0=sQuery(id+"F4.wireOp",EDGE,"E39.MirrorCS");var subQ1=makeQuery(id+"F3.opExtrude","CAP_EDGE",EDGE,{"disambiguationData":[OSD([sQuery(id+"F2.wireOp",EDGE,"E23.MirrorCS")])],"isStart":true});var subQ2=makeQuery(id+"F4.imprint","INTERSECT",VERTEX,{"derivedFrom":[subQ1,subQ0]});Q45=makeQuery(id+"F4.imprint","IMPRINT",FACE,{"disambiguationData":[TD([[makeQuery(id+"F4.imprint","IMPRINT",EDGE,{"disambiguationData":[TD([[subQ2,-1.0]])],"derivedFrom":subQ0}),-1.0]])]});}
            var Q46;
            {var subQ0=sQuery(id+"F4.wireOp",EDGE,"E39.MirrorCS");var subQ1=makeQuery(id+"F3.opExtrude","CAP_EDGE",EDGE,{"disambiguationData":[OSD([sQuery(id+"F2.wireOp",EDGE,"E21.MirrorCS")])],"isStart":true});var subQ2=makeQuery(id+"F4.imprint","INTERSECT",VERTEX,{"derivedFrom":[subQ1,subQ0]});Q46=makeQuery(id+"F4.imprint","IMPRINT",FACE,{"disambiguationData":[TD([[makeQuery(id+"F4.imprint","IMPRINT",EDGE,{"disambiguationData":[TD([[subQ2,-1.0]])],"derivedFrom":subQ0}),-1.0]])]});}
            var Q47;
            {var subQ0=sQuery(id+"F4.wireOp",EDGE,"E39.MirrorCS");var subQ1=makeQuery(id+"F3.opExtrude","CAP_EDGE",EDGE,{"disambiguationData":[OSD([sQuery(id+"F2.wireOp",EDGE,"E19.MirrorCS")])],"isStart":true});var subQ2=makeQuery(id+"F4.imprint","INTERSECT",VERTEX,{"derivedFrom":[subQ1,subQ0]});Q47=makeQuery(id+"F4.imprint","IMPRINT",FACE,{"disambiguationData":[TD([[makeQuery(id+"F4.imprint","IMPRINT",EDGE,{"disambiguationData":[TD([[subQ2,-1.0]])],"derivedFrom":subQ0}),-1.0]])]});}
            var Q48;
            {var subQ0=sQuery(id+"F4.wireOp",EDGE,"E39.MirrorCS");var subQ1=makeQuery(id+"F3.opExtrude","CAP_EDGE",EDGE,{"disambiguationData":[OSD([sQuery(id+"F2.wireOp",EDGE,"E17.MirrorCS")])],"isStart":true});var subQ2=makeQuery(id+"F4.imprint","INTERSECT",VERTEX,{"derivedFrom":[subQ1,subQ0]});Q48=makeQuery(id+"F4.imprint","IMPRINT",FACE,{"disambiguationData":[TD([[makeQuery(id+"F4.imprint","IMPRINT",EDGE,{"disambiguationData":[TD([[subQ2,-1.0]])],"derivedFrom":subQ0}),-1.0]])]});}
            var Q49;
            {var subQ0=sQuery(id+"F4.wireOp",EDGE,"E39.MirrorCS");var subQ1=makeQuery(id+"F3.opExtrude","CAP_EDGE",EDGE,{"disambiguationData":[OSD([sQuery(id+"F2.wireOp",EDGE,"E15.MirrorCS")])],"isStart":true});var subQ2=makeQuery(id+"F4.imprint","INTERSECT",VERTEX,{"derivedFrom":[subQ1,subQ0]});Q49=makeQuery(id+"F4.imprint","IMPRINT",FACE,{"disambiguationData":[TD([[makeQuery(id+"F4.imprint","IMPRINT",EDGE,{"disambiguationData":[TD([[subQ2,-1.0]])],"derivedFrom":subQ0}),-1.0]])]});}
            var Q50;
            {var subQ0=sQuery(id+"F4.wireOp",EDGE,"E39.MirrorCS");var subQ1=makeQuery(id+"F3.opExtrude","CAP_EDGE",EDGE,{"disambiguationData":[OSD([sQuery(id+"F2.wireOp",EDGE,"E12")])],"isStart":true});var subQ2=makeQuery(id+"F4.imprint","INTERSECT",VERTEX,{"derivedFrom":[subQ1,subQ0]});Q50=makeQuery(id+"F4.imprint","IMPRINT",FACE,{"disambiguationData":[TD([[makeQuery(id+"F4.imprint","IMPRINT",EDGE,{"disambiguationData":[TD([[subQ2,-1.0]])],"derivedFrom":subQ0}),-1.0]])]});}
            var Q51;
            {var subQ0=sQuery(id+"F4.wireOp",EDGE,"E39.MirrorCS");var subQ1=makeQuery(id+"F3.opExtrude","CAP_EDGE",EDGE,{"disambiguationData":[OSD([sQuery(id+"F2.wireOp",EDGE,"E14.1.0.0")])],"isStart":true});var subQ2=makeQuery(id+"F4.imprint","INTERSECT",VERTEX,{"derivedFrom":[subQ1,subQ0]});Q51=makeQuery(id+"F4.imprint","IMPRINT",FACE,{"disambiguationData":[TD([[makeQuery(id+"F4.imprint","IMPRINT",EDGE,{"disambiguationData":[TD([[subQ2,-1.0]])],"derivedFrom":subQ0}),-1.0]])]});}
            var Q52;
            {var subQ0=sQuery(id+"F4.wireOp",EDGE,"E39.MirrorCS");var subQ1=makeQuery(id+"F3.opExtrude","CAP_EDGE",EDGE,{"disambiguationData":[OSD([sQuery(id+"F2.wireOp",EDGE,"E14.2.0.0")])],"isStart":true});var subQ2=makeQuery(id+"F4.imprint","INTERSECT",VERTEX,{"derivedFrom":[subQ1,subQ0]});Q52=makeQuery(id+"F4.imprint","IMPRINT",FACE,{"disambiguationData":[TD([[makeQuery(id+"F4.imprint","IMPRINT",EDGE,{"disambiguationData":[TD([[subQ2,-1.0]])],"derivedFrom":subQ0}),-1.0]])]});}
            var Q53;
            {var subQ0=sQuery(id+"F4.wireOp",EDGE,"E39.MirrorCS");var subQ1=makeQuery(id+"F3.opExtrude","CAP_EDGE",EDGE,{"disambiguationData":[OSD([sQuery(id+"F2.wireOp",EDGE,"E14.3.0.0")])],"isStart":true});var subQ2=makeQuery(id+"F4.imprint","INTERSECT",VERTEX,{"derivedFrom":[subQ1,subQ0]});Q53=makeQuery(id+"F4.imprint","IMPRINT",FACE,{"disambiguationData":[TD([[makeQuery(id+"F4.imprint","IMPRINT",EDGE,{"disambiguationData":[TD([[subQ2,-1.0]])],"derivedFrom":subQ0}),-1.0]])]});}
            var Q54;
            {var subQ0=sQuery(id+"F4.wireOp",EDGE,"E39.MirrorCS");var subQ1=makeQuery(id+"F3.opExtrude","CAP_EDGE",EDGE,{"disambiguationData":[OSD([sQuery(id+"F2.wireOp",EDGE,"E14.4.0.0")])],"isStart":true});var subQ2=makeQuery(id+"F4.imprint","INTERSECT",VERTEX,{"derivedFrom":[subQ1,subQ0]});Q54=makeQuery(id+"F4.imprint","IMPRINT",FACE,{"disambiguationData":[TD([[makeQuery(id+"F4.imprint","IMPRINT",EDGE,{"disambiguationData":[TD([[subQ2,-1.0]])],"derivedFrom":subQ0}),-1.0]])]});}
            var Q55;
            {var subQ0=sQuery(id+"F4.wireOp",EDGE,"E39.MirrorCS");var subQ1=makeQuery(id+"F3.opExtrude","CAP_EDGE",EDGE,{"disambiguationData":[OSD([sQuery(id+"F2.wireOp",EDGE,"E14.5.0.0")])],"isStart":true});var subQ2=makeQuery(id+"F4.imprint","INTERSECT",VERTEX,{"derivedFrom":[subQ1,subQ0]});Q55=makeQuery(id+"F4.imprint","IMPRINT",FACE,{"disambiguationData":[TD([[makeQuery(id+"F4.imprint","IMPRINT",EDGE,{"disambiguationData":[TD([[subQ2,-1.0]])],"derivedFrom":subQ0}),-1.0]])]});}
            var Q56;
            {var subQ0=sQuery(id+"F4.wireOp",EDGE,"E39.MirrorCS");var subQ1=makeQuery(id+"F3.opExtrude","CAP_EDGE",EDGE,{"disambiguationData":[OSD([sQuery(id+"F2.wireOp",EDGE,"E14.6.0.0")])],"isStart":true});var subQ2=makeQuery(id+"F4.imprint","INTERSECT",VERTEX,{"derivedFrom":[subQ1,subQ0]});Q56=makeQuery(id+"F4.imprint","IMPRINT",FACE,{"disambiguationData":[TD([[makeQuery(id+"F4.imprint","IMPRINT",EDGE,{"disambiguationData":[TD([[subQ2,-1.0]])],"derivedFrom":subQ0}),-1.0]])]});}
            var Q57;
            {var subQ0=sQuery(id+"F4.wireOp",EDGE,"E39.MirrorCS");var subQ1=makeQuery(id+"F3.opExtrude","CAP_EDGE",EDGE,{"disambiguationData":[OSD([sQuery(id+"F2.wireOp",EDGE,"E14.7.0.0")])],"isStart":true});var subQ2=makeQuery(id+"F4.imprint","INTERSECT",VERTEX,{"derivedFrom":[subQ1,subQ0]});Q57=makeQuery(id+"F4.imprint","IMPRINT",FACE,{"disambiguationData":[TD([[makeQuery(id+"F4.imprint","IMPRINT",EDGE,{"disambiguationData":[TD([[subQ2,-1.0]])],"derivedFrom":subQ0}),-1.0]])]});}
            var Q58;
            {var subQ0=sQuery(id+"F4.wireOp",EDGE,"E39.MirrorCS");var subQ1=makeQuery(id+"F3.opExtrude","CAP_EDGE",EDGE,{"disambiguationData":[OSD([sQuery(id+"F2.wireOp",EDGE,"E14.8.0.0")])],"isStart":true});var subQ2=makeQuery(id+"F4.imprint","INTERSECT",VERTEX,{"derivedFrom":[subQ1,subQ0]});Q58=makeQuery(id+"F4.imprint","IMPRINT",FACE,{"disambiguationData":[TD([[makeQuery(id+"F4.imprint","IMPRINT",EDGE,{"disambiguationData":[TD([[subQ2,-1.0]])],"derivedFrom":subQ0}),-1.0]])]});}
            var Q59;
            {var subQ0=sQuery(id+"F4.wireOp",EDGE,"E46");Q59=makeQuery(id+"F4.imprint","IMPRINT",FACE,{"disambiguationData":[TD([[makeQuery(id+"F4.imprint","IMPRINT",EDGE,{"derivedFrom":subQ0}),1.0]])]});}
            extrude(context, id + "F5", {"entities" : qUnion([Q0, Q1, Q2, Q3, Q4, Q5, Q6, Q7, Q8, Q9, Q10, Q11, Q12, Q13, Q14, Q15, Q16, Q17, Q18, Q19, Q20, Q21, Q22, Q23, Q24, Q25, Q26, Q27, Q28, Q29, Q30, Q31, Q32, Q33, Q34, Q35, Q36, Q37, Q38, Q39, Q40, Q41, Q42, Q43, Q44, Q45, Q46, Q47, Q48, Q49, Q50, Q51, Q52, Q53, Q54, Q55, Q56, Q57, Q58, Q59]), "oppositeDirection" : true, "depth" : 0.5 * mm});
        }
        {
            var Q0;
            Q0=makeQuery(id+"F1.opExtrude","CAP_EDGE",EDGE,{"disambiguationData":[OSD([sQuery(id+"F0.wireOp",EDGE,"E0.right"),sQuery(id+"F0.wireOp",EDGE,"E7")])],"isStart":false});
            var Q1;
            Q1=makeQuery(id+"F1.opExtrude","CAP_EDGE",EDGE,{"disambiguationData":[OSD([sQuery(id+"F0.wireOp",EDGE,"E0.right"),sQuery(id+"F0.wireOp",EDGE,"E7")])],"isStart":true});
            var Q2;
            Q2=makeQuery(id+"F1.opExtrude","CAP_EDGE",EDGE,{"disambiguationData":[OSD([sQuery(id+"F0.wireOp",EDGE,"E9.trimOffspring")])],"isStart":false});
            var Q3;
            Q3=makeQuery(id+"F1.opExtrude","CAP_EDGE",EDGE,{"disambiguationData":[OSD([sQuery(id+"F0.wireOp",EDGE,"E9.trimOffspring")])],"isStart":true});
            var Q4;
            Q4=makeQuery(id+"F1.opExtrude","CAP_EDGE",EDGE,{"disambiguationData":[OSD([sQuery(id+"F0.wireOp",EDGE,"E0.bottom")])],"isStart":false});
            var Q5;
            Q5=makeQuery(id+"F1.opExtrude","CAP_EDGE",EDGE,{"disambiguationData":[OSD([sQuery(id+"F0.wireOp",EDGE,"E0.bottom")])],"isStart":true});
            var Q6;
            Q6=makeQuery(id+"F1.opExtrude","CAP_EDGE",EDGE,{"disambiguationData":[OSD([sQuery(id+"F0.wireOp",EDGE,"E0.left"),sQuery(id+"F0.wireOp",EDGE,"E1")])],"isStart":false});
            var Q7;
            Q7=makeQuery(id+"F1.opExtrude","CAP_EDGE",EDGE,{"disambiguationData":[OSD([sQuery(id+"F0.wireOp",EDGE,"E0.left"),sQuery(id+"F0.wireOp",EDGE,"E1")])],"isStart":true});
            var Q8;
            Q8=makeQuery(id+"F1.opExtrude","CAP_EDGE",EDGE,{"disambiguationData":[OSD([sQuery(id+"F0.wireOp",EDGE,"E3")])],"isStart":true});
            var Q9;
            Q9=makeQuery(id+"F1.opExtrude","CAP_EDGE",EDGE,{"disambiguationData":[OSD([sQuery(id+"F0.wireOp",EDGE,"E3")])],"isStart":false});
            var Q10;
            Q10=makeQuery(id+"F1.opExtrude","CAP_EDGE",EDGE,{"disambiguationData":[OSD([sQuery(id+"F0.wireOp",EDGE,"E0.top")])],"isStart":false});
            var Q11;
            Q11=makeQuery(id+"F1.opExtrude","CAP_EDGE",EDGE,{"disambiguationData":[OSD([sQuery(id+"F0.wireOp",EDGE,"E0.top")])],"isStart":true});
            fillet(context, id + "F6", {"entities" : qUnion([Q0, Q1, Q2, Q3, Q4, Q5, Q6, Q7, Q8, Q9, Q10, Q11]), "radius" : 0.5 * mm, "tangentPropagation" : true, "allowEdgeOverflow" : false});
        }
        {
            var Q0;
            Q0=qCreatedBy(makeId("Top.planeOp"),FACE);
            var sketch = newSketch(context, id + "F7", { "sketchPlane" : qUnion([Q0])});
            skLineSegment(sketch, "E47", {"start": v(0, 0) * mm, "end": v(0, -20) * mm, "construction": true});
            skLineSegment(sketch, "E48", {"start": v(0, -20) * mm, "end": v(-20, -20) * mm, "construction": true});
            skLineSegment(sketch, "E49", {"start": v(-20, -20) * mm, "end": v(-20, 0) * mm});
            skLineSegment(sketch, "E50", {"start": v(-20, 0) * mm, "end": v(-28, 0) * mm});
            skLineSegment(sketch, "E51", {"start": v(-28, 0) * mm, "end": v(-28, -20) * mm});
            skLineSegment(sketch, "E52", {"start": v(-28, -20) * mm, "end": v(-20, -20) * mm});
            skLineSegment(sketch, "E53", {"start": v(-28, -10) * mm, "end": v(-20, -10) * mm, "construction": true});
            skLineSegment(sketch, "E54", {"start": v(-20, -10) * mm, "end": v(-21, -10) * mm, "construction": true});
            skLineSegment(sketch, "E55", {"start": v(-21, -10) * mm, "end": v(-21, -1) * mm, "construction": true});
            skLineSegment(sketch, "E56", {"start": v(-27, -10) * mm, "end": v(-27, -1) * mm, "construction": true});
            skLineSegment(sketch, "E57.MirrorCS", {"start": v(-21, -10) * mm, "end": v(-21, -19) * mm, "construction": true});
            skLineSegment(sketch, "E58.MirrorCS", {"start": v(-27, -10) * mm, "end": v(-27, -19) * mm, "construction": true});
            skCircle(sketch, "E59", {"center": v(-21, -1) * mm, "radius": 0.5 * mm});
            skCircle(sketch, "E60", {"center": v(-27, -1) * mm, "radius": 0.5 * mm});
            skCircle(sketch, "E61", {"center": v(-21, -10) * mm, "radius": 0.5 * mm});
            skCircle(sketch, "E62", {"center": v(-27, -10) * mm, "radius": 0.5 * mm});
            skCircle(sketch, "E63", {"center": v(-21, -19) * mm, "radius": 0.5 * mm});
            skCircle(sketch, "E64", {"center": v(-27, -19) * mm, "radius": 0.5 * mm});
            skSolve(sketch);
        }
        {
            var Q0;
            Q0 = qSketchRegion(id + "F7", true);
            extrude(context, id + "F8", {"entities" : qUnion([Q0]), "depth" : 5 * mm});
        }
        {
            var Q0;
            Q0=makeQuery(id+"F8.opExtrude","SWEPT_FACE",FACE,{"disambiguationData":[OSD([sQuery(id+"F7.wireOp",EDGE,"E51")])]});
            var sketch = newSketch(context, id + "F9", { "sketchPlane" : qUnion([Q0])});
            skLineSegment(sketch, "E65", {"start": v(2, 5) * mm, "end": v(4, 3) * mm});
            skLineSegment(sketch, "E66", {"start": v(4, 3) * mm, "end": v(7, 3) * mm});
            skLineSegment(sketch, "E67", {"start": v(7, 3) * mm, "end": v(9, 5) * mm});
            skLineSegment(sketch, "E68", {"start": v(10, 0) * mm, "end": v(10, 5) * mm, "construction": true});
            skLineSegment(sketch, "E69.MirrorCS", {"start": v(13, 3) * mm, "end": v(11, 5) * mm});
            skLineSegment(sketch, "E70.MirrorCS", {"start": v(16, 3) * mm, "end": v(13, 3) * mm});
            skLineSegment(sketch, "E71.MirrorCS", {"start": v(18, 5) * mm, "end": v(16, 3) * mm});
            skSolve(sketch);
        }
        {
            var Q0;
            {var subQ0=sQuery(id+"F9.wireOp",EDGE,"E65");Q0=makeQuery(id+"F9.imprint","IMPRINT",FACE,{"disambiguationData":[TD([[makeQuery(id+"F9.imprint","IMPRINT",EDGE,{"derivedFrom":subQ0}),1.0]])]});}
            var Q1;
            {var subQ0=sQuery(id+"F9.wireOp",EDGE,"E69.MirrorCS");Q1=makeQuery(id+"F9.imprint","IMPRINT",FACE,{"disambiguationData":[TD([[makeQuery(id+"F9.imprint","IMPRINT",EDGE,{"derivedFrom":subQ0}),-1.0]])]});}
            extrude(context, id + "F10", {"entities" : qUnion([Q0, Q1]), "operationType" : NewBodyOperationType.REMOVE, "oppositeDirection" : true, "depth" : 25 * mm});
        }
    });
